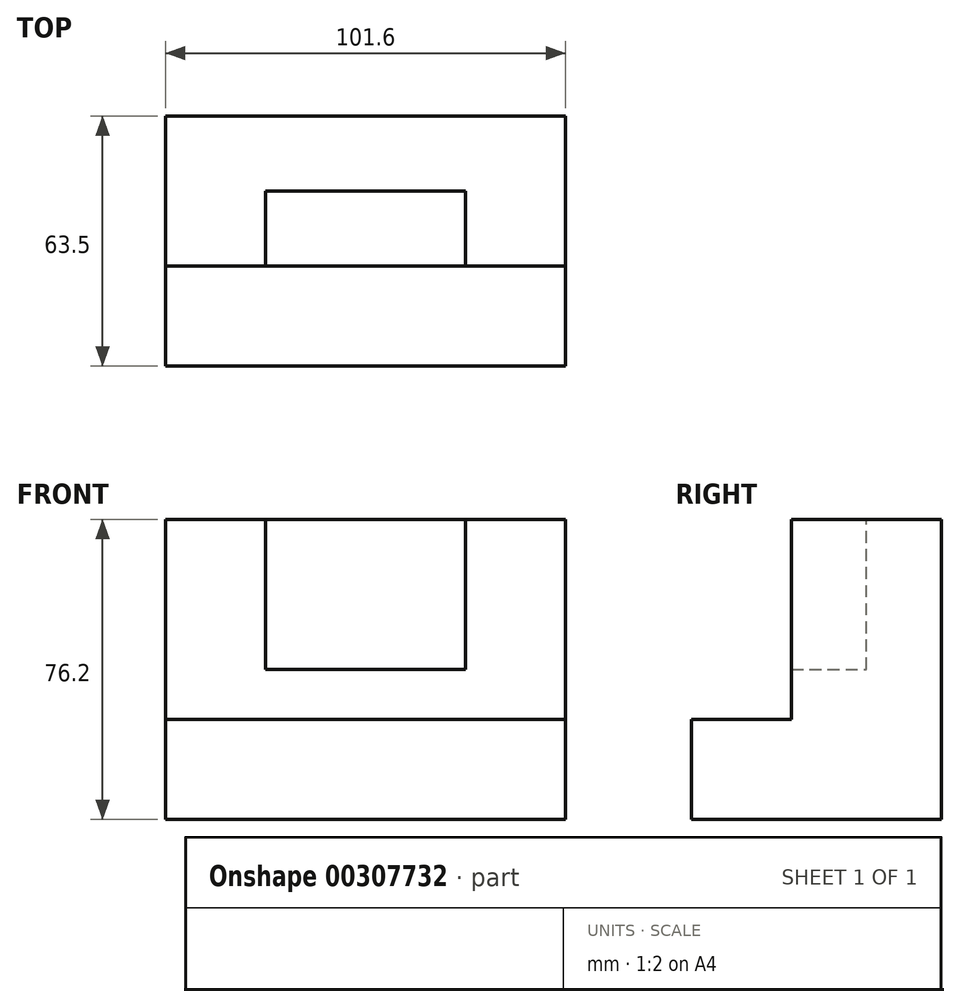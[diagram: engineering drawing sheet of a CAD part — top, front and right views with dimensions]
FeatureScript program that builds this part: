
annotation { "Feature Type Name" : "Feature", "Feature Type Description" : "" }
export const myFeature = defineFeature(function(context is Context, id is Id, definition is map)
    precondition{}
    {
        {
            var Q0;
            Q0=qCreatedBy(makeId("Top.planeOp"),FACE);
            var sketch = newSketch(context, id + "F0", { "sketchPlane" : qUnion([Q0])});
            skLineSegment(sketch, "E0", {"start": v(-41.51, -41.35) * mm, "end": v(60.09, -41.35) * mm});
            skLineSegment(sketch, "E1", {"start": v(60.09, -41.35) * mm, "end": v(60.09, 22.15) * mm});
            skLineSegment(sketch, "E2", {"start": v(60.09, 22.15) * mm, "end": v(-41.51, 22.15) * mm});
            skLineSegment(sketch, "E3", {"start": v(-41.51, 22.15) * mm, "end": v(-41.51, -41.35) * mm});
            skSolve(sketch);
        }
        {
            var Q0;
            Q0=makeQuery(id+"F0.imprint","IMPRINT",FACE,{"disambiguationData":[TD([[makeQuery(id+"F0.imprint","IMPRINT",EDGE,{"derivedFrom":sQuery(id+"F0.wireOp",EDGE,"E0")}),1.0]])]});
            extrude(context, id + "F1", {"entities" : qUnion([Q0]), "depth" : 25.4 * mm});
        }
        {
            var Q0;
            Q0=makeQuery(id+"F1.opExtrude","CAP_FACE",FACE,{"disambiguationData":[OSD([sQuery(id+"F0.wireOp",EDGE,"E0"),sQuery(id+"F0.wireOp",EDGE,"E1"),sQuery(id+"F0.wireOp",EDGE,"E2"),sQuery(id+"F0.wireOp",EDGE,"E3")])],"isStart":false});
            var sketch = newSketch(context, id + "F2", { "sketchPlane" : qUnion([Q0])});
            skLineSegment(sketch, "E4", {"start": v(60.09, 22.15) * mm, "end": v(60.09, -15.95) * mm});
            skLineSegment(sketch, "E5", {"start": v(60.09, -15.95) * mm, "end": v(-41.51, -15.95) * mm});
            skLineSegment(sketch, "E6", {"start": v(-41.51, -15.95) * mm, "end": v(-41.51, 22.15) * mm});
            skLineSegment(sketch, "E7", {"start": v(-41.51, 22.15) * mm, "end": v(60.09, 22.15) * mm});
            skSolve(sketch);
        }
        {
            var Q0;
            Q0=makeQuery(id+"F2.imprint","IMPRINT",FACE,{"disambiguationData":[TD([[makeQuery(id+"F2.imprint","IMPRINT",EDGE,{"derivedFrom":sQuery(id+"F2.wireOp",EDGE,"E4")}),1.0]])]});
            extrude(context, id + "F3", {"entities" : qUnion([Q0]), "operationType" : NewBodyOperationType.ADD, "depth" : 50.8 * mm});
        }
        {
            var Q0;
            Q0=makeQuery(id+"F3.opExtrude","CAP_FACE",FACE,{"disambiguationData":[OSD([sQuery(id+"F2.wireOp",EDGE,"E4"),sQuery(id+"F2.wireOp",EDGE,"E5"),sQuery(id+"F2.wireOp",EDGE,"E6"),sQuery(id+"F2.wireOp",EDGE,"E7")])],"isStart":false});
            var sketch = newSketch(context, id + "F4", { "sketchPlane" : qUnion([Q0])});
            skLineSegment(sketch, "E8", {"start": v(34.69, -15.95) * mm, "end": v(-16.11, -15.95) * mm});
            skLineSegment(sketch, "E9", {"start": v(-16.11, -15.95) * mm, "end": v(-16.11, 3.1) * mm});
            skLineSegment(sketch, "E10", {"start": v(-16.11, 3.1) * mm, "end": v(34.69, 3.1) * mm});
            skLineSegment(sketch, "E11", {"start": v(34.69, 3.1) * mm, "end": v(34.69, -15.95) * mm});
            skSolve(sketch);
        }
        {
            var Q0;
            Q0=makeQuery(id+"F4.imprint","IMPRINT",FACE,{"disambiguationData":[TD([[makeQuery(id+"F4.imprint","IMPRINT",EDGE,{"derivedFrom":sQuery(id+"F4.wireOp",EDGE,"E9")}),-1.0]])]});
            extrude(context, id + "F5", {"entities" : qUnion([Q0]), "operationType" : NewBodyOperationType.REMOVE, "oppositeDirection" : true, "depth" : 38.1 * mm});
        }
    });
